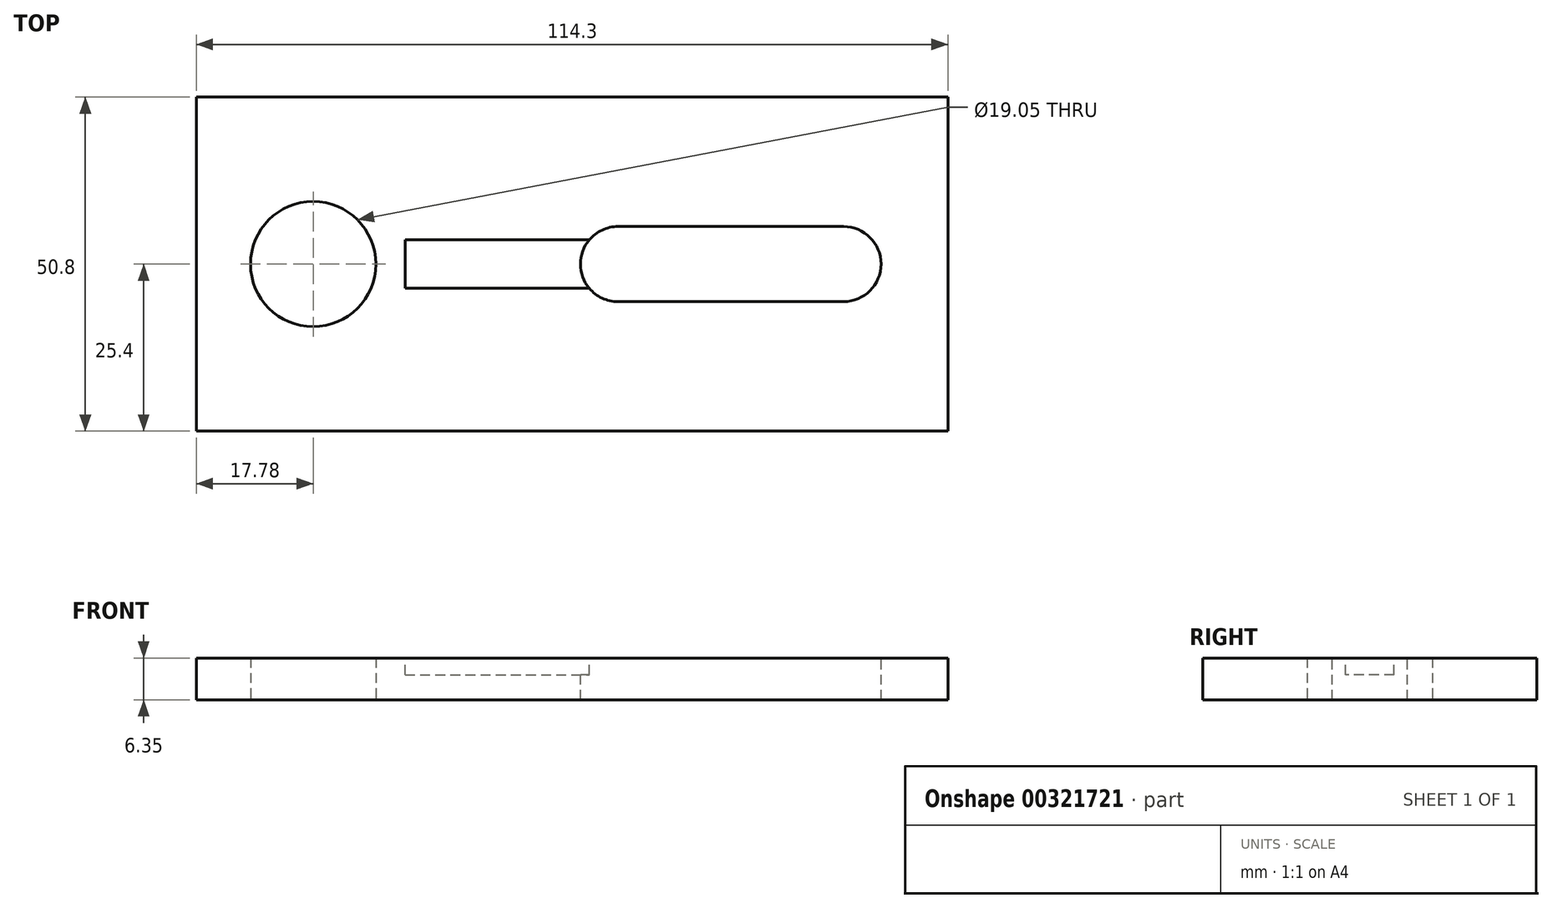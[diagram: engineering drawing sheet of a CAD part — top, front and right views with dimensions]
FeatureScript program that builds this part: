
annotation { "Feature Type Name" : "Feature", "Feature Type Description" : "" }
export const myFeature = defineFeature(function(context is Context, id is Id, definition is map)
    precondition{}
    {
        {
            var Q0;
            Q0=qCreatedBy(makeId("Top.planeOp"),FACE);
            var sketch = newSketch(context, id + "F0", { "sketchPlane" : qUnion([Q0])});
            skLineSegment(sketch, "E0.bottom", {"start": v(0, 0) * mm, "end": v(-114.3, 0) * mm});
            skLineSegment(sketch, "E0.top", {"start": v(0, 50.8) * mm, "end": v(-114.3, 50.8) * mm});
            skLineSegment(sketch, "E0.left", {"start": v(0, 0) * mm, "end": v(0, 50.8) * mm});
            skLineSegment(sketch, "E0.right", {"start": v(-114.3, 0) * mm, "end": v(-114.3, 50.8) * mm});
            skCircle(sketch, "E1", {"center": v(-96.52, 25.4) * mm, "radius": 9.53 * mm});
            skSolve(sketch);
        }
        {
            var Q0;
            Q0=makeQuery(id+"F0.imprint","IMPRINT",FACE,{"disambiguationData":[TD([[makeQuery(id+"F0.imprint","IMPRINT",EDGE,{"derivedFrom":sQuery(id+"F0.wireOp",EDGE,"E0.bottom")}),-1.0]])]});
            extrude(context, id + "F1", {"entities" : qUnion([Q0]), "depth" : 6.35 * mm});
        }
        {
            var Q0;
            Q0=makeQuery(id+"F1.opExtrude","CAP_FACE",FACE,{"disambiguationData":[OSD([sQuery(id+"F0.wireOp",EDGE,"E0.bottom"),sQuery(id+"F0.wireOp",EDGE,"E0.top"),sQuery(id+"F0.wireOp",EDGE,"E0.left"),sQuery(id+"F0.wireOp",EDGE,"E0.right"),sQuery(id+"F0.wireOp",EDGE,"E1")])],"isStart":false});
            var sketch = newSketch(context, id + "F2", { "sketchPlane" : qUnion([Q0])});
            skLineSegment(sketch, "E2.bottom", {"start": v(-15.88, 31.12) * mm, "end": v(-50.17, 31.12) * mm});
            skLineSegment(sketch, "E2.top", {"start": v(-15.88, 19.69) * mm, "end": v(-50.17, 19.69) * mm});
            skLineSegment(sketch, "E2.left", {"start": v(-15.88, 31.12) * mm, "end": v(-15.88, 19.69) * mm});
            skLineSegment(sketch, "E2.right", {"start": v(-50.17, 31.12) * mm, "end": v(-50.17, 19.69) * mm});
            skPoint(sketch, "E2.middle", {"position": v(-33.02, 25.4) * mm});
            skArc(sketch, "E3", {"start": v(-50.17, 31.12) * mm, "mid": v(-55.88, 25.4) * mm, "end": v(-50.17, 19.69) * mm});
            skArc(sketch, "E4", {"start": v(-15.88, 31.12) * mm, "mid": v(-10.16, 25.4) * mm, "end": v(-15.88, 19.69) * mm});
            skSolve(sketch);
        }
        {
            var Q0;
            Q0=makeQuery(id+"F2.imprint","IMPRINT",FACE,{"disambiguationData":[TD([[makeQuery(id+"F2.imprint","IMPRINT",EDGE,{"derivedFrom":sQuery(id+"F2.wireOp",EDGE,"E2.bottom")}),1.0]])]});
            var Q1;
            Q1=makeQuery(id+"F2.imprint","IMPRINT",FACE,{"disambiguationData":[TD([[makeQuery(id+"F2.imprint","IMPRINT",EDGE,{"derivedFrom":sQuery(id+"F2.wireOp",EDGE,"E2.right")}),-1.0]])]});
            var Q2;
            Q2=makeQuery(id+"F2.imprint","IMPRINT",FACE,{"disambiguationData":[TD([[makeQuery(id+"F2.imprint","IMPRINT",EDGE,{"derivedFrom":sQuery(id+"F2.wireOp",EDGE,"E2.left")}),1.0]])]});
            extrude(context, id + "F3", {"entities" : qUnion([Q0, Q1, Q2]), "operationType" : NewBodyOperationType.REMOVE, "oppositeDirection" : true, "depth" : 25.4 * mm});
        }
        {
            var Q0;
            Q0=makeQuery(id+"F1.opExtrude","CAP_FACE",FACE,{"disambiguationData":[OSD([sQuery(id+"F0.wireOp",EDGE,"E0.bottom"),sQuery(id+"F0.wireOp",EDGE,"E0.top"),sQuery(id+"F0.wireOp",EDGE,"E0.left"),sQuery(id+"F0.wireOp",EDGE,"E0.right"),sQuery(id+"F0.wireOp",EDGE,"E1")])],"isStart":false});
            var sketch = newSketch(context, id + "F4", { "sketchPlane" : qUnion([Q0])});
            skLineSegment(sketch, "E5.bottom", {"start": v(-82.55, 29.08) * mm, "end": v(-29.21, 29.08) * mm});
            skLineSegment(sketch, "E5.top", {"start": v(-82.55, 21.72) * mm, "end": v(-29.21, 21.72) * mm});
            skLineSegment(sketch, "E5.left", {"start": v(-82.55, 29.08) * mm, "end": v(-82.55, 21.72) * mm});
            skLineSegment(sketch, "E5.right", {"start": v(-29.21, 29.08) * mm, "end": v(-29.21, 21.72) * mm});
            skPoint(sketch, "E5.middle", {"position": v(-55.88, 25.4) * mm});
            skSolve(sketch);
        }
        {
            var Q0;
            {var subQ0=sQuery(id+"F4.wireOp",EDGE,"E5.left");Q0=makeQuery(id+"F4.imprint","IMPRINT",FACE,{"disambiguationData":[TD([[makeQuery(id+"F4.imprint","IMPRINT",EDGE,{"derivedFrom":subQ0}),1.0]])]});}
            extrude(context, id + "F5", {"entities" : qUnion([Q0]), "operationType" : NewBodyOperationType.REMOVE, "oppositeDirection" : true, "depth" : 2.54 * mm});
        }
    });
